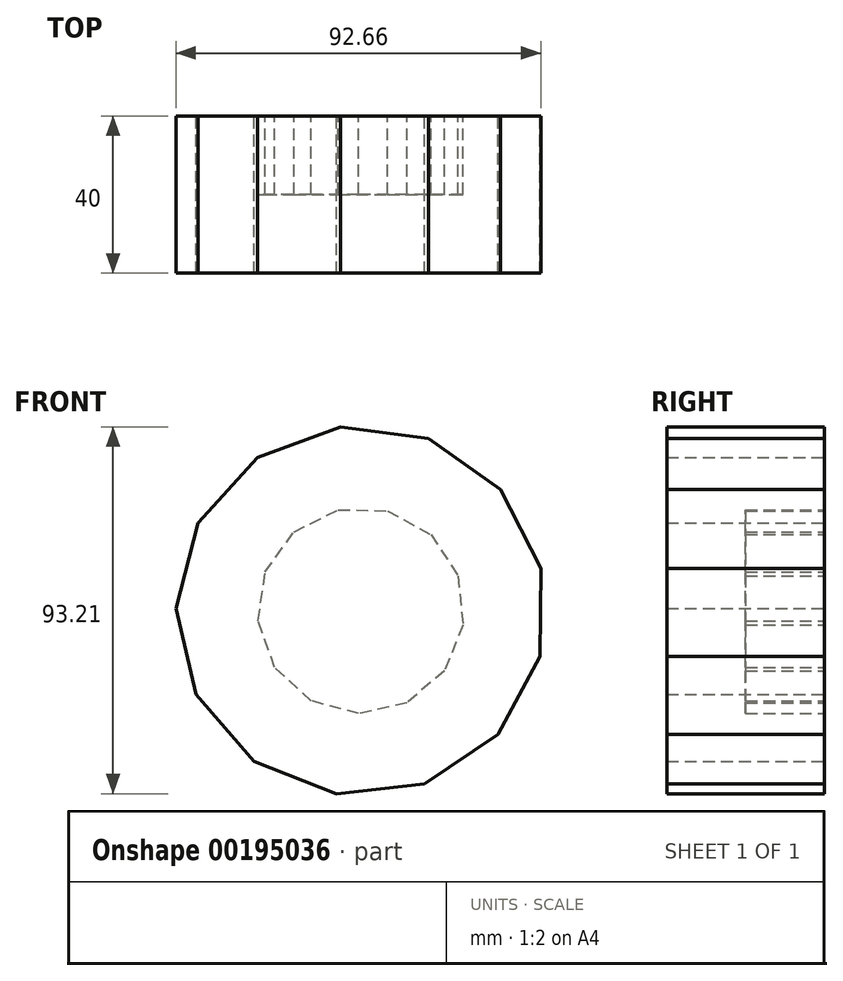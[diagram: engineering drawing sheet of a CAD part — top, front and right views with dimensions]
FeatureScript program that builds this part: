
annotation { "Feature Type Name" : "Feature", "Feature Type Description" : "" }
export const myFeature = defineFeature(function(context is Context, id is Id, definition is map)
    precondition{}
    {
        {
            var Q0;
            Q0=qCreatedBy(makeId("Front.planeOp"),FACE);
            var sketch = newSketch(context, id + "F0", { "sketchPlane" : qUnion([Q0])});
            skLineSegment(sketch, "E0.0", {"start": v(34.8, -31.52) * mm, "end": v(16.17, -44.08) * mm});
            skLineSegment(sketch, "E0.1", {"start": v(16.17, -44.08) * mm, "end": v(-6.17, -46.54) * mm});
            skLineSegment(sketch, "E0.2", {"start": v(-6.17, -46.54) * mm, "end": v(-27.1, -38.34) * mm});
            skLineSegment(sketch, "E0.3", {"start": v(-27.1, -38.34) * mm, "end": v(-41.81, -21.36) * mm});
            skLineSegment(sketch, "E0.4", {"start": v(-41.81, -21.36) * mm, "end": v(-46.95, 0.52) * mm});
            skLineSegment(sketch, "E0.5", {"start": v(-46.95, 0.52) * mm, "end": v(-41.33, 22.28) * mm});
            skLineSegment(sketch, "E0.6", {"start": v(-41.33, 22.28) * mm, "end": v(-26.25, 38.93) * mm});
            skLineSegment(sketch, "E0.7", {"start": v(-26.25, 38.93) * mm, "end": v(-5.15, 46.67) * mm});
            skLineSegment(sketch, "E0.8", {"start": v(-5.15, 46.67) * mm, "end": v(17.13, 43.71) * mm});
            skLineSegment(sketch, "E0.9", {"start": v(17.13, 43.71) * mm, "end": v(35.48, 30.75) * mm});
            skLineSegment(sketch, "E0.10", {"start": v(35.48, 30.75) * mm, "end": v(45.7, 10.73) * mm});
            skLineSegment(sketch, "E0.11", {"start": v(45.7, 10.73) * mm, "end": v(45.46, -11.74) * mm});
            skLineSegment(sketch, "E0.12", {"start": v(45.46, -11.74) * mm, "end": v(34.8, -31.52) * mm});
            skLineSegment(sketch, "E1.0", {"start": v(11.7, -23.45) * mm, "end": v(-0.53, -26.2) * mm});
            skLineSegment(sketch, "E1.1", {"start": v(-0.53, -26.2) * mm, "end": v(-12.65, -22.95) * mm});
            skLineSegment(sketch, "E1.2", {"start": v(-12.65, -22.95) * mm, "end": v(-21.87, -14.44) * mm});
            skLineSegment(sketch, "E1.3", {"start": v(-21.87, -14.44) * mm, "end": v(-26.08, -2.63) * mm});
            skLineSegment(sketch, "E1.4", {"start": v(-26.08, -2.63) * mm, "end": v(-24.3, 9.8) * mm});
            skLineSegment(sketch, "E1.5", {"start": v(-24.3, 9.8) * mm, "end": v(-16.97, 19.97) * mm});
            skLineSegment(sketch, "E1.6", {"start": v(-16.97, 19.97) * mm, "end": v(-5.75, 25.57) * mm});
            skLineSegment(sketch, "E1.7", {"start": v(-5.75, 25.57) * mm, "end": v(6.79, 25.31) * mm});
            skLineSegment(sketch, "E1.8", {"start": v(6.79, 25.31) * mm, "end": v(17.78, 19.26) * mm});
            skLineSegment(sketch, "E1.9", {"start": v(17.78, 19.26) * mm, "end": v(24.69, 8.8) * mm});
            skLineSegment(sketch, "E1.10", {"start": v(24.69, 8.8) * mm, "end": v(25.95, -3.69) * mm});
            skLineSegment(sketch, "E1.11", {"start": v(25.95, -3.69) * mm, "end": v(21.26, -15.32) * mm});
            skLineSegment(sketch, "E1.12", {"start": v(21.26, -15.32) * mm, "end": v(11.7, -23.45) * mm});
            skSolve(sketch);
        }
        {
            var Q0;
            Q0=makeQuery(id+"F0.imprint","IMPRINT",FACE,{"disambiguationData":[TD([[makeQuery(id+"F0.imprint","IMPRINT",EDGE,{"derivedFrom":sQuery(id+"F0.wireOp",EDGE,"E0.0")}),-1.0]])]});
            extrude(context, id + "F1", {"entities" : qUnion([Q0]), "endBound" : BoundingType.SYMMETRIC, "depth" : 40 * mm});
        }
        {
            var Q0;
            Q0=makeQuery(id+"F0.imprint","IMPRINT",FACE,{"disambiguationData":[TD([[makeQuery(id+"F0.imprint","IMPRINT",EDGE,{"derivedFrom":sQuery(id+"F0.wireOp",EDGE,"E1.0")}),-1.0]])]});
            extrude(context, id + "F2", {"entities" : qUnion([Q0]), "operationType" : NewBodyOperationType.ADD, "depth" : 20 * mm});
        }
    });
